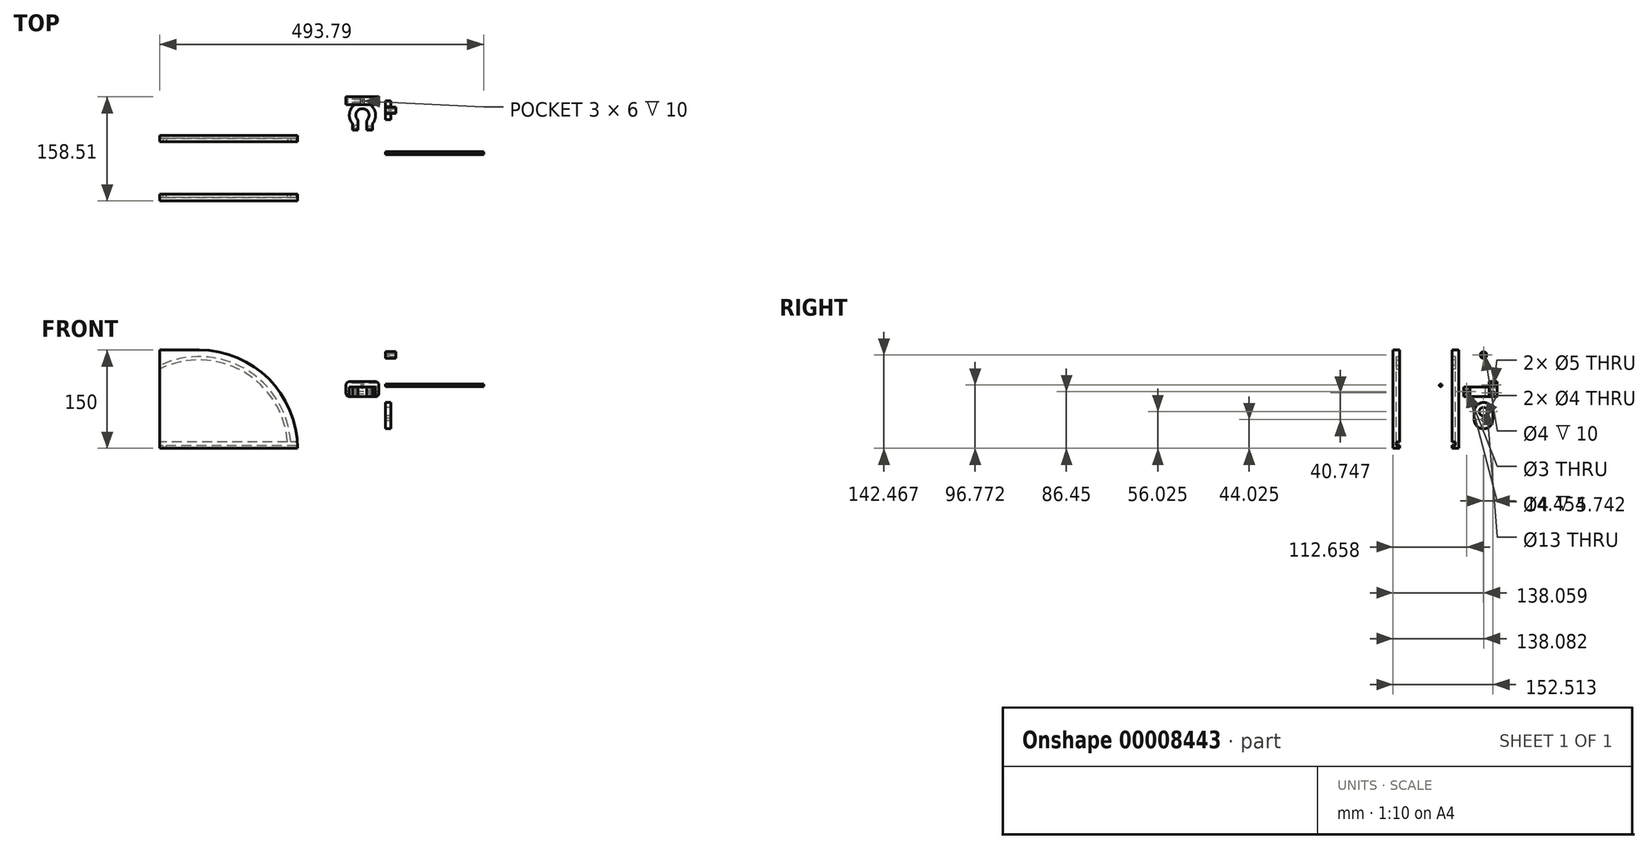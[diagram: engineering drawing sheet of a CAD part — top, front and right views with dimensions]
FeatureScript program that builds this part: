
annotation { "Feature Type Name" : "Feature", "Feature Type Description" : "" }
export const myFeature = defineFeature(function(context is Context, id is Id, definition is map)
    precondition{}
    {
        {
            var Q0;
            Q0=qCreatedBy(makeId("Top.planeOp"),FACE);
            var sketch = newSketch(context, id + "F0", { "sketchPlane" : qUnion([Q0])});
            skArc(sketch, "E0", {"start": v(-24.65, 30.51) * mm, "mid": v(-34.75, 40.61) * mm, "end": v(-44.85, 30.51) * mm});
            skArc(sketch, "E1", {"start": v(-44.85, 30.51) * mm, "mid": v(-44.24, 27.06) * mm, "end": v(-42.49, 24.02) * mm});
            skArc(sketch, "E2", {"start": v(-27.01, 24.02) * mm, "mid": v(-25.26, 27.06) * mm, "end": v(-24.65, 30.51) * mm});
            skArc(sketch, "E3", {"start": v(-14.75, 30.51) * mm, "mid": v(-34.75, 50.51) * mm, "end": v(-54.75, 30.51) * mm});
            skArc(sketch, "E4", {"start": v(-54.75, 30.51) * mm, "mid": v(-53.54, 23.67) * mm, "end": v(-50.07, 17.66) * mm});
            skArc(sketch, "E5", {"start": v(-19.43, 17.66) * mm, "mid": v(-15.96, 23.67) * mm, "end": v(-14.75, 30.51) * mm});
            skLineSegment(sketch, "E6", {"start": v(-50.07, 17.66) * mm, "end": v(-34.75, 30.51) * mm, "construction": true});
            skLineSegment(sketch, "E7", {"start": v(-34.75, 30.51) * mm, "end": v(-19.43, 17.66) * mm, "construction": true});
            skArc(sketch, "E8", {"start": v(-50.07, 17.66) * mm, "mid": v(-43.1, 17.05) * mm, "end": v(-42.49, 24.02) * mm});
            skArc(sketch, "E9", {"start": v(-27.01, 24.02) * mm, "mid": v(-26.4, 17.05) * mm, "end": v(-19.43, 17.66) * mm});
            skLineSegment(sketch, "E10", {"start": v(-46.75, 46.51) * mm, "end": v(-22.75, 46.51) * mm});
            skPoint(sketch, "E11", {"position": v(-34.75, 46.51) * mm});
            skLineSegment(sketch, "E12", {"start": v(-50.07, 17.66) * mm, "end": v(-50.07, 7.66) * mm});
            skLineSegment(sketch, "E13", {"start": v(-50.07, 7.66) * mm, "end": v(-41.33, 7.66) * mm});
            skLineSegment(sketch, "E14", {"start": v(-41.33, 7.66) * mm, "end": v(-41.33, 20.84) * mm});
            skLineSegment(sketch, "E15", {"start": v(-28.17, 20.84) * mm, "end": v(-28.17, 7.66) * mm});
            skLineSegment(sketch, "E16", {"start": v(-28.17, 7.66) * mm, "end": v(-19.43, 7.66) * mm});
            skLineSegment(sketch, "E17", {"start": v(-19.43, 7.66) * mm, "end": v(-19.43, 17.66) * mm});
            skSolve(sketch);
        }
        {
            var Q0;
            Q0=makeQuery(id+"F0.imprint","IMPRINT",FACE,{"disambiguationData":[TD([[makeQuery(id+"F0.imprint","IMPRINT",EDGE,{"derivedFrom":sQuery(id+"F0.wireOp",EDGE,"E0")}),-1.0]])]});
            var Q1;
            {var subQ0=sQuery(id+"F0.wireOp",EDGE,"E12");Q1=makeQuery(id+"F0.imprint","IMPRINT",FACE,{"disambiguationData":[TD([[makeQuery(id+"F0.imprint","IMPRINT",EDGE,{"derivedFrom":subQ0}),1.0]])]});}
            var Q2;
            {var subQ0=sQuery(id+"F0.wireOp",EDGE,"E15");Q2=makeQuery(id+"F0.imprint","IMPRINT",FACE,{"disambiguationData":[TD([[makeQuery(id+"F0.imprint","IMPRINT",EDGE,{"derivedFrom":subQ0}),1.0]])]});}
            extrude(context, id + "F1", {"entities" : qUnion([Q0, Q1, Q2]), "depth" : 15 * mm});
        }
        {
            var Q0;
            Q0=makeQuery(id+"F1.opExtrude","SWEPT_FACE",FACE,{"disambiguationData":[OSD([sQuery(id+"F0.wireOp",EDGE,"E17")])]});
            var sketch = newSketch(context, id + "F2", { "sketchPlane" : qUnion([Q0])});
            skPoint(sketch, "E18", {"position": v(17.66, 0) * mm});
            skPoint(sketch, "E19", {"position": v(12.66, 0) * mm});
            skPoint(sketch, "E20", {"position": v(7.66, 0) * mm});
            skPoint(sketch, "E21", {"position": v(7.66, 15) * mm});
            skPoint(sketch, "E22", {"position": v(17.66, 15) * mm});
            skPoint(sketch, "E23", {"position": v(17.66, 7.5) * mm});
            skCircle(sketch, "E24", {"center": v(12.66, 7.5) * mm, "radius": 1.5 * mm});
            skSolve(sketch);
        }
        {
            var Q0;
            Q0=makeQuery(id+"F2.imprint","IMPRINT",FACE,{"disambiguationData":[TD([[makeQuery(id+"F2.imprint","IMPRINT",EDGE,{"derivedFrom":sQuery(id+"F2.wireOp",EDGE,"E24")}),1.0]])]});
            var Q1;
            Q1=sQuery(id+"F2.wireOp",EDGE,"E24");
            extrude(context, id + "F3", {"entities" : qUnion([Q0]), "operationType" : NewBodyOperationType.REMOVE, "surfaceEntities" : qUnion([Q1]), "endBound" : BoundingType.UP_TO_NEXT, "oppositeDirection" : true, "depth" : 25 * mm});
        }
        {
            var Q0;
            Q0=makeQuery(id+"F1.opExtrude","SWEPT_FACE",FACE,{"disambiguationData":[OSD([sQuery(id+"F0.wireOp",EDGE,"E12")])]});
            var sketch = newSketch(context, id + "F4", { "sketchPlane" : qUnion([Q0])});
            skPoint(sketch, "E25", {"position": v(-17.66, 15) * mm});
            skPoint(sketch, "E26", {"position": v(-7.66, 15) * mm});
            skPoint(sketch, "E27", {"position": v(-12.66, 15) * mm});
            skPoint(sketch, "E28", {"position": v(-7.66, 0) * mm});
            skPoint(sketch, "E29", {"position": v(-7.66, 7.5) * mm});
            skPoint(sketch, "E30", {"position": v(-12.66, 7.5) * mm});
            skCircle(sketch, "E31.cCircle", {"center": v(-12.66, 7.5) * mm, "radius": 3 * mm, "construction": true});
            skLineSegment(sketch, "E31.0", {"start": v(-15.66, 5.77) * mm, "end": v(-15.66, 9.23) * mm});
            skLineSegment(sketch, "E31.1", {"start": v(-15.66, 9.23) * mm, "end": v(-12.66, 10.96) * mm});
            skLineSegment(sketch, "E31.2", {"start": v(-12.66, 10.96) * mm, "end": v(-9.66, 9.23) * mm});
            skLineSegment(sketch, "E31.3", {"start": v(-9.66, 9.23) * mm, "end": v(-9.66, 5.77) * mm});
            skLineSegment(sketch, "E31.4", {"start": v(-9.66, 5.77) * mm, "end": v(-12.66, 4.04) * mm});
            skLineSegment(sketch, "E31.5", {"start": v(-12.66, 4.04) * mm, "end": v(-15.66, 5.77) * mm});
            skPoint(sketch, "E31.0.midPoint", {"position": v(-15.66, 7.5) * mm});
            skSolve(sketch);
        }
        {
            var Q0;
            Q0=makeQuery(id+"F4.imprint","IMPRINT",FACE,{"disambiguationData":[TD([[makeQuery(id+"F4.imprint","IMPRINT",EDGE,{"derivedFrom":sQuery(id+"F4.wireOp",EDGE,"E31.0")}),-1.0]])]});
            extrude(context, id + "F5", {"entities" : qUnion([Q0]), "operationType" : NewBodyOperationType.REMOVE, "oppositeDirection" : true, "depth" : 3 * mm});
        }
        {
            var Q0;
            Q0=makeQuery(id+"F1.opExtrude","SWEPT_FACE",FACE,{"disambiguationData":[OSD([sQuery(id+"F0.wireOp",EDGE,"E10")])]});
            var sketch = newSketch(context, id + "F6", { "sketchPlane" : qUnion([Q0])});
            skPoint(sketch, "E32", {"position": v(22.75, 15) * mm});
            skPoint(sketch, "E33", {"position": v(22.75, 0) * mm});
            skPoint(sketch, "E34", {"position": v(46.75, 0) * mm});
            skPoint(sketch, "E35", {"position": v(46.75, 15) * mm});
            skPoint(sketch, "E36", {"position": v(46.75, 7.5) * mm});
            skPoint(sketch, "E37", {"position": v(34.75, 15) * mm});
            skPoint(sketch, "E38", {"position": v(34.75, 0) * mm});
            skPoint(sketch, "E39", {"position": v(22.75, 7.5) * mm});
            skPoint(sketch, "E40", {"position": v(34.75, 7.5) * mm});
            skLineSegment(sketch, "E41.bottom", {"start": v(14.75, 22.82) * mm, "end": v(54.75, 22.82) * mm});
            skLineSegment(sketch, "E41.top", {"start": v(14.75, 0) * mm, "end": v(54.75, 0) * mm});
            skLineSegment(sketch, "E41.left", {"start": v(9.75, 17.82) * mm, "end": v(9.75, 5) * mm});
            skLineSegment(sketch, "E41.right", {"start": v(59.75, 17.82) * mm, "end": v(59.75, 5) * mm});
            skPoint(sketch, "E42.visualSharp", {"position": v(9.75, 22.82) * mm});
            skArc(sketch, "E42.filletArc", {"start": v(14.75, 22.82) * mm, "mid": v(11.21, 21.36) * mm, "end": v(9.75, 17.82) * mm});
            skPoint(sketch, "E43.visualSharp", {"position": v(59.75, 22.82) * mm});
            skArc(sketch, "E43.filletArc", {"start": v(59.75, 17.82) * mm, "mid": v(58.29, 21.36) * mm, "end": v(54.75, 22.82) * mm});
            skPoint(sketch, "E44.visualSharp", {"position": v(9.75, 0) * mm});
            skArc(sketch, "E44.filletArc", {"start": v(9.75, 5) * mm, "mid": v(11.21, 1.46) * mm, "end": v(14.75, 0) * mm});
            skPoint(sketch, "E45.visualSharp", {"position": v(59.75, 0) * mm});
            skArc(sketch, "E45.filletArc", {"start": v(54.75, 0) * mm, "mid": v(58.29, 1.46) * mm, "end": v(59.75, 5) * mm});
            skSolve(sketch);
        }
        {
            var Q0;
            Q0=makeQuery(id+"F6.imprint","IMPRINT",FACE,{"disambiguationData":[TD([[makeQuery(id+"F6.imprint","IMPRINT",EDGE,{"derivedFrom":sQuery(id+"F6.wireOp",EDGE,"E41.bottom")}),-1.0]])]});
            var Q1;
            {var subQ0=sQuery(id+"F0.wireOp",EDGE,"E10");Q1=makeQuery(id+"F6.imprint","IMPRINT",FACE,{"disambiguationData":[TD([[makeQuery(id+"F6.imprint","IMPRINT",EDGE,{"derivedFrom":makeQuery(id+"F1.opExtrude","CAP_EDGE",EDGE,{"disambiguationData":[OSD([subQ0])],"isStart":false})}),1.0]])]});}
            extrude(context, id + "F7", {"entities" : qUnion([Q0, Q1]), "operationType" : NewBodyOperationType.ADD, "depth" : 12 * mm});
        }
        {
            var Q0;
            Q0=makeQuery(id+"F7.opExtrude","SWEPT_FACE",FACE,{"disambiguationData":[OSD([sQuery(id+"F6.wireOp",EDGE,"E41.right")])]});
            var sketch = newSketch(context, id + "F8", { "sketchPlane" : qUnion([Q0])});
            skPoint(sketch, "E46", {"position": v(-58.51, 17.82) * mm});
            skPoint(sketch, "E47", {"position": v(-46.51, 17.82) * mm});
            skPoint(sketch, "E48", {"position": v(-52.51, 17.82) * mm});
            skPoint(sketch, "E49", {"position": v(-46.51, 5) * mm});
            skPoint(sketch, "E50", {"position": v(-46.51, 11.41) * mm});
            skPoint(sketch, "E51", {"position": v(-52.51, 5.82) * mm});
            skCircle(sketch, "E52", {"center": v(-52.51, 5.82) * mm, "radius": 2 * mm});
            skCircle(sketch, "E53", {"center": v(-52.51, 17.82) * mm, "radius": 2.5 * mm});
            skSolve(sketch);
        }
        {
            var Q0;
            {var subQ0=makeQuery(id+"F7.opExtrude","SWEPT_EDGE",EDGE,{"disambiguationData":[OSD([sQuery(id+"F6.wireOp",EDGE,"E41.right"),sQuery(id+"F6.wireOp",EDGE,"E43.filletArc")])]});var subQ1=sQuery(id+"F8.wireOp",EDGE,"E53");var subQ3=makeQuery(id+"F8.imprint","INTERSECT",VERTEX,{"disambiguationData":[OD(0.0)],"derivedFrom":[subQ0,subQ1]});Q0=makeQuery(id+"F8.imprint","IMPRINT",FACE,{"disambiguationData":[TD([[makeQuery(id+"F8.imprint","IMPRINT",EDGE,{"disambiguationData":[TD([[subQ3,-1.0]])],"derivedFrom":subQ1}),1.0]])]});}
            var Q1;
            {var subQ0=makeQuery(id+"F7.opExtrude","SWEPT_EDGE",EDGE,{"disambiguationData":[OSD([sQuery(id+"F6.wireOp",EDGE,"E41.right"),sQuery(id+"F6.wireOp",EDGE,"E43.filletArc")])]});var subQ1=sQuery(id+"F8.wireOp",EDGE,"E53");var subQ3=makeQuery(id+"F8.imprint","INTERSECT",VERTEX,{"disambiguationData":[OD(0.0)],"derivedFrom":[subQ0,subQ1]});Q1=makeQuery(id+"F8.imprint","IMPRINT",FACE,{"disambiguationData":[TD([[makeQuery(id+"F8.imprint","IMPRINT",EDGE,{"disambiguationData":[TD([[subQ3,1.0]])],"derivedFrom":subQ1}),1.0]])]});}
            var Q2;
            Q2=makeQuery(id+"F8.imprint","IMPRINT",FACE,{"disambiguationData":[TD([[makeQuery(id+"F8.imprint","IMPRINT",EDGE,{"derivedFrom":sQuery(id+"F8.wireOp",EDGE,"E52")}),1.0]])]});
            extrude(context, id + "F9", {"entities" : qUnion([Q0, Q1, Q2]), "operationType" : NewBodyOperationType.REMOVE, "endBound" : BoundingType.THROUGH_ALL, "oppositeDirection" : true, "depth" : 25 * mm});
        }
        {
            var Q0;
            Q0=makeQuery(id+"F7.opExtrude","SWEPT_FACE",FACE,{"disambiguationData":[OSD([sQuery(id+"F6.wireOp",EDGE,"E41.bottom")])]});
            var sketch = newSketch(context, id + "F10", { "sketchPlane" : qUnion([Q0])});
            skPoint(sketch, "E54", {"position": v(-54.75, 58.51) * mm});
            skPoint(sketch, "E55", {"position": v(-54.75, 46.51) * mm});
            skPoint(sketch, "E56", {"position": v(-14.75, 46.51) * mm});
            skPoint(sketch, "E57", {"position": v(-14.75, 58.51) * mm});
            skPoint(sketch, "E58", {"position": v(-34.75, 58.51) * mm});
            skPoint(sketch, "E59", {"position": v(-34.75, 46.51) * mm});
            skPoint(sketch, "E60", {"position": v(-54.75, 52.51) * mm});
            skPoint(sketch, "E61", {"position": v(-14.75, 52.51) * mm});
            skLineSegment(sketch, "E62.bottom", {"start": v(-36.25, 55.51) * mm, "end": v(-33.25, 55.51) * mm});
            skLineSegment(sketch, "E62.top", {"start": v(-36.25, 49.51) * mm, "end": v(-33.25, 49.51) * mm});
            skLineSegment(sketch, "E62.left", {"start": v(-36.25, 55.51) * mm, "end": v(-36.25, 49.51) * mm});
            skLineSegment(sketch, "E62.right", {"start": v(-33.25, 55.51) * mm, "end": v(-33.25, 49.51) * mm});
            skPoint(sketch, "E63", {"position": v(-34.75, 55.51) * mm});
            skPoint(sketch, "E64", {"position": v(-33.25, 52.51) * mm});
            skSolve(sketch);
        }
        {
            var Q0;
            Q0=makeQuery(id+"F10.imprint","IMPRINT",FACE,{"disambiguationData":[TD([[makeQuery(id+"F10.imprint","IMPRINT",EDGE,{"derivedFrom":sQuery(id+"F10.wireOp",EDGE,"E62.bottom")}),-1.0]])]});
            extrude(context, id + "F11", {"entities" : qUnion([Q0]), "operationType" : NewBodyOperationType.REMOVE, "oppositeDirection" : true, "depth" : 10 * mm});
        }
        {
            var Q0;
            Q0=qCreatedBy(makeId("Right.planeOp"),FACE);
            var sketch = newSketch(context, id + "F12", { "sketchPlane" : qUnion([Q0])});
            skCircle(sketch, "E65", {"center": v(-27.3, 17.24) * mm, "radius": 2 * mm});
            skSolve(sketch);
        }
        {
            var Q0;
            Q0=makeQuery(id+"F12.imprint","IMPRINT",FACE,{"disambiguationData":[TD([[makeQuery(id+"F12.imprint","IMPRINT",EDGE,{"derivedFrom":sQuery(id+"F12.wireOp",EDGE,"E65")}),1.0]])]});
            extrude(context, id + "F13", {"entities" : qUnion([Q0]), "depth" : 150 * mm});
        }
        {
            var Q0;
            Q0=qCreatedBy(makeId("Right.planeOp"),FACE);
            var sketch = newSketch(context, id + "F14", { "sketchPlane" : qUnion([Q0])});
            skCircle(sketch, "E66", {"center": v(38.06, -34.93) * mm, "radius": 2 * mm});
            skCircle(sketch, "E67", {"center": v(38.06, -22.93) * mm, "radius": 6.5 * mm});
            skArc(sketch, "E68", {"start": v(52.13, -22.93) * mm, "mid": v(38.06, -8.85) * mm, "end": v(23.99, -22.93) * mm});
            skArc(sketch, "E69", {"start": v(23.99, -34.93) * mm, "mid": v(38.06, -49) * mm, "end": v(52.13, -34.93) * mm});
            skLineSegment(sketch, "E70", {"start": v(52.13, -34.93) * mm, "end": v(52.13, -22.93) * mm});
            skLineSegment(sketch, "E71", {"start": v(23.99, -22.93) * mm, "end": v(23.99, -34.93) * mm});
            skSolve(sketch);
        }
        {
            var Q0;
            Q0=makeQuery(id+"F14.imprint","IMPRINT",FACE,{"disambiguationData":[TD([[makeQuery(id+"F14.imprint","IMPRINT",EDGE,{"derivedFrom":sQuery(id+"F14.wireOp",EDGE,"E66")}),-1.0]])]});
            extrude(context, id + "F15", {"entities" : qUnion([Q0]), "depth" : 8.5 * mm});
        }
        {
            var Q0;
            Q0=qCreatedBy(makeId("Right.planeOp"),FACE);
            var sketch = newSketch(context, id + "F16", { "sketchPlane" : qUnion([Q0])});
            skCircle(sketch, "E72", {"center": v(38.08, 63.52) * mm, "radius": 5 * mm});
            skSolve(sketch);
        }
        {
            var Q0;
            Q0=makeQuery(id+"F16.imprint","IMPRINT",FACE,{"disambiguationData":[TD([[makeQuery(id+"F16.imprint","IMPRINT",EDGE,{"derivedFrom":sQuery(id+"F16.wireOp",EDGE,"E72")}),1.0]])]});
            var Q1;
            Q1=sQuery(id+"F16.wireOp",EDGE,"E72");
            extrude(context, id + "F17", {"entities" : qUnion([Q0]), "surfaceEntities" : qUnion([Q1]), "depth" : 16 * mm});
        }
        {
            var Q0;
            Q0=makeQuery(id+"F17.opExtrude","CAP_FACE",FACE,{"disambiguationData":[OSD([sQuery(id+"F16.wireOp",EDGE,"E72")])],"isStart":true});
            var sketch = newSketch(context, id + "F18", { "sketchPlane" : qUnion([Q0])});
            skPoint(sketch, "E73", {"position": v(-38.08, 63.52) * mm});
            skCircle(sketch, "E74", {"center": v(-38.08, 63.52) * mm, "radius": 3 * mm});
            skLineSegment(sketch, "E75", {"start": v(-40.68, 65.02) * mm, "end": v(-35.48, 65.02) * mm});
            skLineSegment(sketch, "E76", {"start": v(-35.48, 62.02) * mm, "end": v(-40.68, 62.02) * mm});
            skSolve(sketch);
        }
        {
            var Q0;
            {var subQ1=sQuery(id+"F18.wireOp",EDGE,"E75");Q0=makeQuery(id+"F18.imprint","IMPRINT",FACE,{"disambiguationData":[TD([[makeQuery(id+"F18.imprint","IMPRINT",EDGE,{"derivedFrom":subQ1}),-1.0]])]});}
            extrude(context, id + "F19", {"entities" : qUnion([Q0]), "operationType" : NewBodyOperationType.REMOVE, "oppositeDirection" : true, "depth" : 6 * mm});
        }
        {
            var Q0;
            Q0=makeQuery(id+"F17.opExtrude","CAP_FACE",FACE,{"disambiguationData":[OSD([sQuery(id+"F16.wireOp",EDGE,"E72")])],"isStart":false});
            var sketch = newSketch(context, id + "F20", { "sketchPlane" : qUnion([Q0])});
            skCircle(sketch, "E77", {"center": v(38.08, 63.52) * mm, "radius": 2 * mm});
            skSolve(sketch);
        }
        {
            var Q0;
            Q0=makeQuery(id+"F20.imprint","IMPRINT",FACE,{"disambiguationData":[TD([[makeQuery(id+"F20.imprint","IMPRINT",EDGE,{"derivedFrom":sQuery(id+"F20.wireOp",EDGE,"E77")}),1.0]])]});
            extrude(context, id + "F21", {"entities" : qUnion([Q0]), "operationType" : NewBodyOperationType.REMOVE, "oppositeDirection" : true, "depth" : 10 * mm});
        }
        {
            var Q0;
            Q0=makeQuery(id+"F5.boolean.opBoolean","COPY",FACE,{"derivedFrom":makeQuery(id+"F5.opExtrude","CAP_FACE",FACE,{"disambiguationData":[OSD([sQuery(id+"F4.wireOp",EDGE,"E31.0"),sQuery(id+"F4.wireOp",EDGE,"E31.1"),sQuery(id+"F4.wireOp",EDGE,"E31.2"),sQuery(id+"F4.wireOp",EDGE,"E31.3"),sQuery(id+"F4.wireOp",EDGE,"E31.4"),sQuery(id+"F4.wireOp",EDGE,"E31.5")])],"isStart":false})});
            var sketch = newSketch(context, id + "F22", { "sketchPlane" : qUnion([Q0])});
            skPoint(sketch, "E78", {"position": v(-12.66, 4.04) * mm});
            skPoint(sketch, "E79", {"position": v(-12.66, 10.96) * mm});
            skPoint(sketch, "E80", {"position": v(-15.66, 9.23) * mm});
            skPoint(sketch, "E81", {"position": v(-9.66, 5.77) * mm});
            skLineSegment(sketch, "E82", {"start": v(-12.66, 10.96) * mm, "end": v(-12.66, 4.04) * mm, "construction": true});
            skLineSegment(sketch, "E83", {"start": v(-9.66, 5.77) * mm, "end": v(-15.66, 9.23) * mm, "construction": true});
            skPoint(sketch, "E84", {"position": v(-12.66, 7.5) * mm});
            skCircle(sketch, "E85", {"center": v(-12.66, 7.5) * mm, "radius": 2 * mm});
            skSolve(sketch);
        }
        {
            var Q0;
            Q0=makeQuery(id+"F22.imprint","IMPRINT",FACE,{"disambiguationData":[TD([[makeQuery(id+"F22.imprint","IMPRINT",EDGE,{"derivedFrom":sQuery(id+"F22.wireOp",EDGE,"E85")}),1.0]])]});
            extrude(context, id + "F23", {"entities" : qUnion([Q0]), "operationType" : NewBodyOperationType.REMOVE, "endBound" : BoundingType.UP_TO_NEXT, "oppositeDirection" : true, "depth" : 25 * mm});
        }
        {
            var Q0;
            Q0=qCreatedBy(makeId("Front.planeOp"),FACE);
            var sketch = newSketch(context, id + "F24", { "sketchPlane" : qUnion([Q0])});
            skLineSegment(sketch, "E86", {"start": v(-343.8, 71.05) * mm, "end": v(-343.8, -78.95) * mm});
            skLineSegment(sketch, "E87", {"start": v(-343.8, -78.95) * mm, "end": v(-133.8, -78.95) * mm});
            skArc(sketch, "E88", {"start": v(-133.8, -78.95) * mm, "mid": v(-177.73, 27.11) * mm, "end": v(-283.8, 71.05) * mm});
            skLineSegment(sketch, "E89", {"start": v(-343.8, 71.05) * mm, "end": v(-283.8, 71.05) * mm});
            skSolve(sketch);
        }
        {
            var Q0;
            Q0=makeQuery(id+"F24.imprint","IMPRINT",FACE,{"disambiguationData":[TD([[makeQuery(id+"F24.imprint","IMPRINT",EDGE,{"derivedFrom":sQuery(id+"F24.wireOp",EDGE,"E86")}),1.0]])]});
            extrude(context, id + "F25", {"entities" : qUnion([Q0]), "depth" : 10 * mm});
        }
        {
            var Q0;
            Q0=makeQuery(id+"F25.opExtrude","CAP_FACE",FACE,{"disambiguationData":[OSD([sQuery(id+"F24.wireOp",EDGE,"E86"),sQuery(id+"F24.wireOp",EDGE,"E87"),sQuery(id+"F24.wireOp",EDGE,"E88"),sQuery(id+"F24.wireOp",EDGE,"E89")])],"isStart":false});
            var sketch = newSketch(context, id + "F26", { "sketchPlane" : qUnion([Q0])});
            skPoint(sketch, "E90", {"position": v(-283.8, -78.95) * mm});
            skArc(sketch, "E91", {"start": v(-143.8, -78.95) * mm, "mid": v(-208.96, 39.37) * mm, "end": v(-343.8, 47.54) * mm});
            skArc(sketch, "E92", {"start": v(-148.8, -78.95) * mm, "mid": v(-212.64, 35.78) * mm, "end": v(-343.8, 41.98) * mm});
            skLineSegment(sketch, "E93", {"start": v(-343.8, 47.54) * mm, "end": v(-343.8, 41.98) * mm});
            skLineSegment(sketch, "E94", {"start": v(-148.8, -78.95) * mm, "end": v(-143.8, -78.95) * mm});
            skLineSegment(sketch, "E95", {"start": v(-134.13, -68.95) * mm, "end": v(-343.8, -68.95) * mm});
            skLineSegment(sketch, "E96", {"start": v(-343.8, -68.95) * mm, "end": v(-343.8, -73.95) * mm});
            skLineSegment(sketch, "E97", {"start": v(-343.8, -73.95) * mm, "end": v(-133.88, -73.95) * mm});
            skArc(sketch, "E98", {"start": v(-133.88, -73.95) * mm, "mid": v(-133.98, -71.45) * mm, "end": v(-134.13, -68.95) * mm});
            skLineSegment(sketch, "E99", {"start": v(-338.8, -78.95) * mm, "end": v(-338.8, 44.34) * mm});
            skLineSegment(sketch, "E100", {"start": v(-333.8, -78.95) * mm, "end": v(-333.8, 46.45) * mm});
            skArc(sketch, "E101", {"start": v(-333.8, 46.45) * mm, "mid": v(-336.3, 45.42) * mm, "end": v(-338.8, 44.34) * mm});
            skSolve(sketch);
        }
        {
            var Q0;
            {var subQ0=sQuery(id+"F26.wireOp",EDGE,"E101");Q0=makeQuery(id+"F26.imprint","IMPRINT",FACE,{"disambiguationData":[TD([[makeQuery(id+"F26.imprint","IMPRINT",EDGE,{"derivedFrom":subQ0}),1.0]])]});}
            var Q1;
            {var subQ6=sQuery(id+"F26.wireOp",EDGE,"E96");Q1=makeQuery(id+"F26.imprint","IMPRINT",FACE,{"disambiguationData":[TD([[makeQuery(id+"F26.imprint","IMPRINT",EDGE,{"derivedFrom":subQ6}),1.0]])]});}
            var Q2;
            {var subQ0=sQuery(id+"F26.wireOp",EDGE,"E100");var subQ3=sQuery(id+"F26.wireOp",EDGE,"E95");var subQ4=makeQuery(id+"F26.imprint","INTERSECT",VERTEX,{"derivedFrom":[subQ3,subQ0]});Q2=makeQuery(id+"F26.imprint","IMPRINT",FACE,{"disambiguationData":[TD([[makeQuery(id+"F26.imprint","IMPRINT",EDGE,{"disambiguationData":[TD([[subQ4,-1.0]])],"derivedFrom":subQ3}),1.0]])]});}
            var Q3;
            {var subQ3=sQuery(id+"F26.wireOp",EDGE,"E99");var subQ5=sQuery(id+"F26.wireOp",EDGE,"E97");var subQ7=makeQuery(id+"F26.imprint","INTERSECT",VERTEX,{"derivedFrom":[subQ5,subQ3]});Q3=makeQuery(id+"F26.imprint","IMPRINT",FACE,{"disambiguationData":[TD([[makeQuery(id+"F26.imprint","IMPRINT",EDGE,{"disambiguationData":[TD([[subQ7,-1.0]])],"derivedFrom":subQ5}),-1.0]])]});}
            var Q4;
            {var subQ1=sQuery(id+"F26.wireOp",EDGE,"E97");var subQ5=sQuery(id+"F26.wireOp",EDGE,"E92");var subQ6=makeQuery(id+"F26.imprint","INTERSECT",VERTEX,{"derivedFrom":[subQ5,subQ1]});Q4=makeQuery(id+"F26.imprint","IMPRINT",FACE,{"disambiguationData":[TD([[makeQuery(id+"F26.imprint","IMPRINT",EDGE,{"disambiguationData":[TD([[subQ6,-1.0]])],"derivedFrom":subQ5}),1.0]])]});}
            var Q5;
            {var subQ6=sQuery(id+"F26.wireOp",EDGE,"E93");Q5=makeQuery(id+"F26.imprint","IMPRINT",FACE,{"disambiguationData":[TD([[makeQuery(id+"F26.imprint","IMPRINT",EDGE,{"derivedFrom":subQ6}),1.0]])]});}
            var Q6;
            {var subQ0=sQuery(id+"F26.wireOp",EDGE,"E97");var subQ3=sQuery(id+"F26.wireOp",EDGE,"E91");var subQ4=makeQuery(id+"F26.imprint","INTERSECT",VERTEX,{"derivedFrom":[subQ3,subQ0]});Q6=makeQuery(id+"F26.imprint","IMPRINT",FACE,{"disambiguationData":[TD([[makeQuery(id+"F26.imprint","IMPRINT",EDGE,{"disambiguationData":[TD([[subQ4,-1.0]])],"derivedFrom":subQ3}),1.0]])]});}
            var Q7;
            {var subQ0=sQuery(id+"F26.wireOp",EDGE,"E98");Q7=makeQuery(id+"F26.imprint","IMPRINT",FACE,{"disambiguationData":[TD([[makeQuery(id+"F26.imprint","IMPRINT",EDGE,{"derivedFrom":subQ0}),1.0]])]});}
            extrude(context, id + "F27", {"entities" : qUnion([Q0, Q1, Q2, Q3, Q4, Q5, Q6, Q7]), "operationType" : NewBodyOperationType.REMOVE, "oppositeDirection" : true, "depth" : 5 * mm});
        }
        {
            var Q0;
            Q0=makeQuery(id+"F25.opExtrude","SWEPT_BODY",BODY,{"disambiguationData":[OSD([sQuery(id+"F24.wireOp",EDGE,"E86"),sQuery(id+"F24.wireOp",EDGE,"E87"),sQuery(id+"F24.wireOp",EDGE,"E88"),sQuery(id+"F24.wireOp",EDGE,"E89")])]});
            var Q1;
            Q1=qCreatedBy(makeId("Front.planeOp"),FACE);
            mirror(context, id + "F28", {"entities" : qUnion([Q0]), "mirrorPlane" : qUnion([Q1])});
        }
        {
            var Q0;
            Q0=makeQuery(id+"F28.opPattern","COPY",BODY,{"derivedFrom":makeQuery(id+"F25.opExtrude","SWEPT_BODY",BODY,{"disambiguationData":[OSD([sQuery(id+"F24.wireOp",EDGE,"E86"),sQuery(id+"F24.wireOp",EDGE,"E87"),sQuery(id+"F24.wireOp",EDGE,"E88"),sQuery(id+"F24.wireOp",EDGE,"E89")])]}),"instanceName":"1"});
            transform(context, id + "F29", {"entities" : qUnion([Q0]), "transformType" : TransformType.TRANSLATION_3D, "dx" : 0 * mm, "dy" : -100 * mm, "dz" : 0 * mm, "makeCopy" : false});
        }
    });
